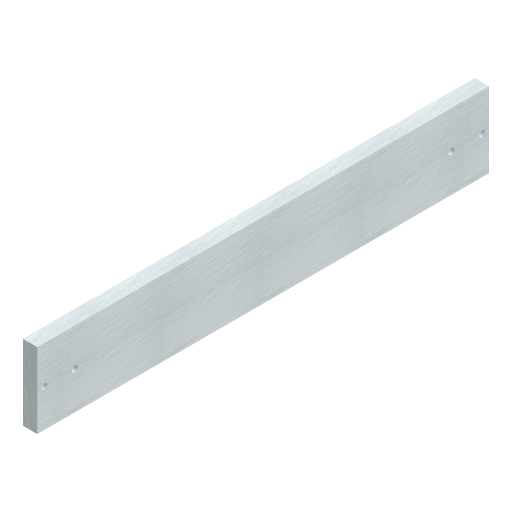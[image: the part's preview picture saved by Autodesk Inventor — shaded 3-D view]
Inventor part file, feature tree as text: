
AUTODESK INVENTOR PART (.ipt)
format: ipt  version: 2024 (Build 280153000, 153)  size: 194,048 bytes
history: native  units: in
note: dims shown in document units (in); Inventor stores cm internally (conversion verified against a paired STEP export)
features: extrude x2, sketch x2
ambient origin geometry x8: Origin, YZ Plane, XZ Plane, XY Plane, X Axis, Y Axis, Z Axis, Center Point
bodies: Solid1 (feature_tree)
feature tree (4):
  extrude  "Extrusion1"  Depth=23.622in
  extrude  "Extrusion2"  Depth=0.374in
  sketch  "Sketch1"  dims[d0=3.937in d1=23.622in]
  sketch  "Sketch2"  dims[d2=0.374in d3=0.374in d4=0.315in d5=0.315in d6=0.748in d7=0.0in d12=1.9685in d13=1.9685in d14=0.315in d15=0.315in d16=0.4331in d17=0.0in]
